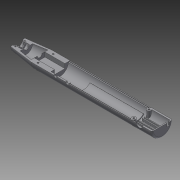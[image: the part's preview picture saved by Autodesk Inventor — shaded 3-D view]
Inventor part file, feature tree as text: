
AUTODESK INVENTOR PART (.ipt)
format: ipt  version: 2014 (Build 180170000, 170)  size: 496,640 bytes
history: native  units: mm
features: extrude x20, sketch x20, other x12, projected_geometry x3, loft x1, fillet x1, mirror x1
ambient origin geometry x8: Origin, YZ Plane, XZ Plane, XY Plane, X Axis, Y Axis, Z Axis, Center Point
bodies: Body1 (feature_tree)
feature tree (58):
  other  "Твердое тело1"
  extrude  "Выдавливание1"  Depth=11.0mm
  other  "РабПлоскость1"
  sketch  "Эскиз3"
  extrude  "Выдавливание2"  Depth=13.0mm
  loft  "Лофт2"
  extrude  "Выдавливание3"  Depth=180.0mm
  extrude  "Выдавливание4"  Depth=9.0mm
  extrude  "Выдавливание_Стойки"  Depth=6.0mm
  other  "РабПлоскость2"
  extrude  "Выдавливание Кнопки"  Depth=1.2mm TaperAngle=0.0deg
  fillet  "Сопряжение Торец копуса"  [1 undecoded]
  other  "РабПлоскость3"
  other  "РабПлоскость8"
  extrude  "Выдавливание8"  TaperAngle=0.0deg  [1 undecoded]
  other  "РабПлоскость7"
  extrude  "Выдавливание9"  Depth=1.5mm
  other  "РабПлоскость6"
  extrude  "Выдавливание11"  Depth=0.8mm
  other  "РабПлоскость5 Середина корпуса"
  extrude  "Выдавливание12"  Depth=1.0mm
  extrude  "Выдавливание13"  Depth=27.0mm TaperAngle=0.0deg
  extrude  "Выдавливание14"  Depth=4.0mm
  extrude  "Выдавливание15"  Depth=3.0mm
  extrude  "Выдавливание16"  Depth=2.0mm TaperAngle=0.0deg
  extrude  "Выдавливание17"  Depth=1.5mm
  extrude  "Выдавливание18"  Depth=5.0mm
  extrude  "Выдавливание19"  Depth=4.0mm
  extrude  "Выдавливание20"  Depth=25.0mm
  extrude  "Выдавливание21"  Depth=120.0mm
  mirror  "Зеркальное отражение1"
  other  "Выступ2"
  other  "Выступ3"
  other  "РабПлоскость9"
  extrude  "Выдавливание22"  Depth=2.0mm
  sketch  "Эскиз1"
  sketch  "Эскиз4"
  other  "Ребра2"
  sketch  "Эскиз5"
  sketch  "Эскиз6"
  sketch  "Эскиз7"
  sketch  "Эскиз8"
  sketch  "Эскиз10"
  sketch  "Эскиз11"
  sketch  "Эскиз14"
  sketch  "Эскиз18"
  sketch  "Эскиз19"
  sketch  "Эскиз20"
  projected_geometry  "Спроецированная петля1"
  sketch  "Эскиз21"
  sketch  "Эскиз22"
  projected_geometry  "Спроецированная петля2"
  sketch  "Эскиз23"
  sketch  "Эскиз24"
  projected_geometry  "Спроецированная петля3"
  sketch  "Эскиз25"
  sketch  "Эскиз26"
  sketch  "Эскиз27"
note: 2 required parameter values undecoded (feature->parameter linkage not recoverable at this tier; creation-order binding heuristic only, values carry confidence <= 0.55)
